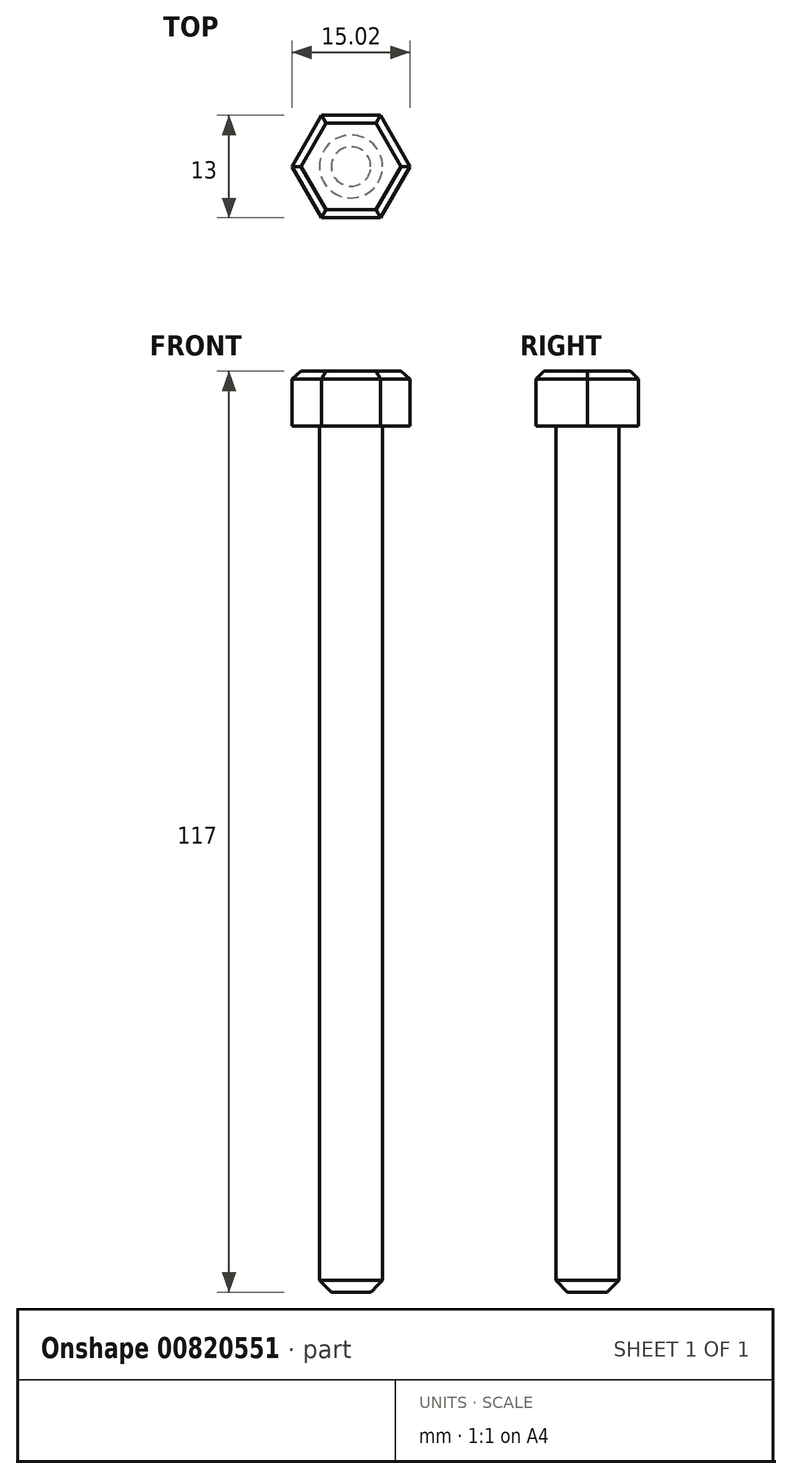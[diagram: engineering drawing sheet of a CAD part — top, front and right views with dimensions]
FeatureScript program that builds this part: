
annotation { "Feature Type Name" : "Feature", "Feature Type Description" : "" }
export const myFeature = defineFeature(function(context is Context, id is Id, definition is map)
    precondition{}
    {
        {
            var Q0;
            Q0=qCreatedBy(makeId("Top.planeOp"),FACE);
            var sketch = newSketch(context, id + "F0", { "sketchPlane" : qUnion([Q0])});
            skCircle(sketch, "E0", {"center": v(0, 0) * mm, "radius": 4 * mm});
            skCircle(sketch, "E1.cCircle", {"center": v(0, 0) * mm, "radius": 6.5 * mm, "construction": true});
            skLineSegment(sketch, "E1.0", {"start": v(-3.75, 6.5) * mm, "end": v(3.75, 6.5) * mm});
            skLineSegment(sketch, "E1.1", {"start": v(3.75, 6.5) * mm, "end": v(7.5, 0) * mm});
            skLineSegment(sketch, "E1.2", {"start": v(7.5, 0) * mm, "end": v(3.75, -6.5) * mm});
            skLineSegment(sketch, "E1.3", {"start": v(3.75, -6.5) * mm, "end": v(-3.75, -6.5) * mm});
            skLineSegment(sketch, "E1.4", {"start": v(-3.75, -6.5) * mm, "end": v(-7.5, 0) * mm});
            skLineSegment(sketch, "E1.5", {"start": v(-7.5, 0) * mm, "end": v(-3.75, 6.5) * mm});
            skPoint(sketch, "E1.0.midPoint", {"position": v(0, 6.5) * mm});
            skSolve(sketch);
        }
        {
            var Q0;
            Q0=qSketchRegion(id+"F0",true);
            var Q1;
            Q1=makeQuery(id+"F0.imprint","IMPRINT",FACE,{"disambiguationData":[TD([[makeQuery(id+"F0.imprint","IMPRINT",EDGE,{"derivedFrom":sQuery(id+"F0.wireOp",EDGE,"E0")}),1.0]])]});
            extrude(context, id + "F1", {"entities" : qUnion([Q0, Q1]), "depth" : 7 * mm, "offsetDistance" : 25 * mm});
        }
        {
            var Q0;
            Q0=makeQuery(id+"F0.imprint","IMPRINT",FACE,{"disambiguationData":[TD([[makeQuery(id+"F0.imprint","IMPRINT",EDGE,{"derivedFrom":sQuery(id+"F0.wireOp",EDGE,"E0")}),1.0]])]});
            extrude(context, id + "F2", {"entities" : qUnion([Q0]), "operationType" : NewBodyOperationType.ADD, "oppositeDirection" : true, "depth" : 110 * mm, "offsetDistance" : 25 * mm});
        }
        {
            var Q0;
            Q0=makeQuery(id+"F2.opExtrude","CAP_EDGE",EDGE,{"disambiguationData":[OSD([sQuery(id+"F0.wireOp",EDGE,"E0")])],"isStart":false});
            chamfer(context, id + "F3", {"entities" : qUnion([Q0]), "width" : 1.5 * mm, "tangentPropagation" : true});
        }
        {
            var Q0;
            Q0=makeQuery(id+"F1.opExtrude","CAP_EDGE",EDGE,{"disambiguationData":[OSD([sQuery(id+"F0.wireOp",EDGE,"E1.1")])],"isStart":false});
            var Q1;
            Q1=makeQuery(id+"F1.opExtrude","CAP_FACE",FACE,{"disambiguationData":[OSD([sQuery(id+"F0.wireOp",EDGE,"E1.0"),sQuery(id+"F0.wireOp",EDGE,"E1.1"),sQuery(id+"F0.wireOp",EDGE,"E1.2"),sQuery(id+"F0.wireOp",EDGE,"E1.3"),sQuery(id+"F0.wireOp",EDGE,"E1.4"),sQuery(id+"F0.wireOp",EDGE,"E1.5")])],"isStart":false});
            chamfer(context, id + "F4", {"entities" : qUnion([Q0, Q1]), "chamferType" : ChamferType.TWO_OFFSETS, "width1" : 1 * mm, "oppositeDirection" : false, "width2" : 1 * mm, "tangentPropagation" : true});
        }
    });
